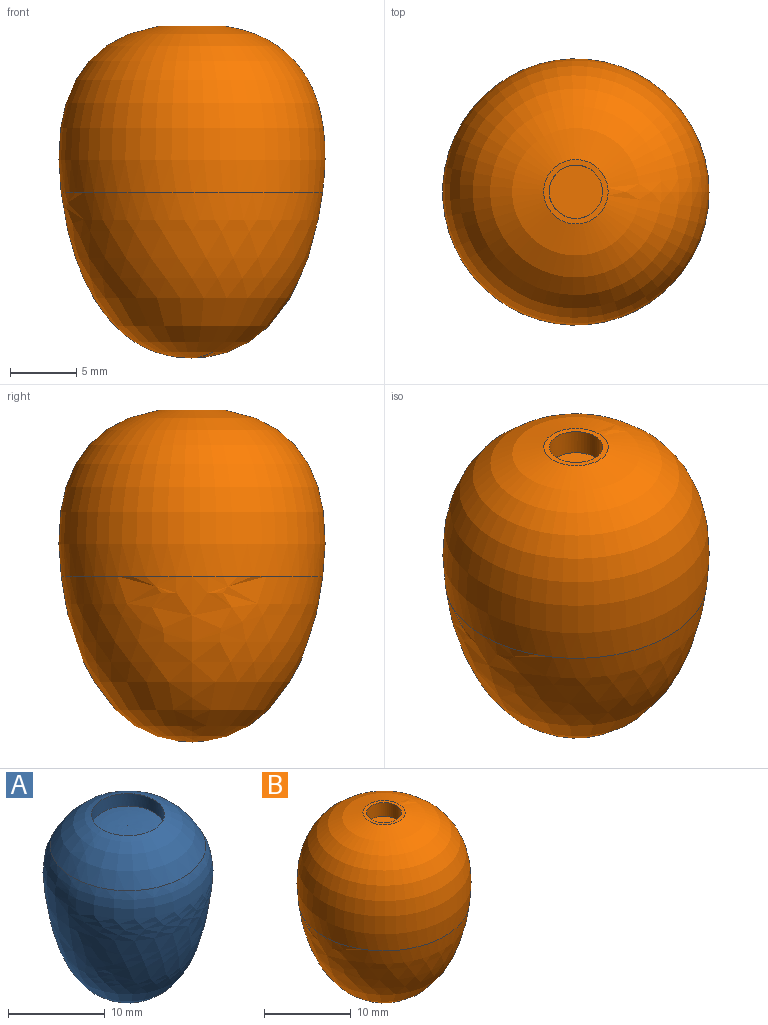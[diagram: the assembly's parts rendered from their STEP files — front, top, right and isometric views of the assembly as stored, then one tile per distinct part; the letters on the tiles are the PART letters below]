
ASSEMBLY  parts=2 mates=1
PART A: 6 faces, bbox 17.6x17.6x22.3 mm
  f0: revolved ~18.32x17.59mm, area 924.4mm2, adj f1
  f1: revolved ~16.06x16.06mm, area 231.2mm2, adj f0,f2
  f2: cylinder r=3.76mm len=7.53mm, axis (0,0,-1), area 37.4mm2, adj f1,f3
  f3: revolved ~7.53x7.53mm, area 44.7mm2, adj f2
  f4: revolved ~13.54x13.54mm, area 369.3mm2, adj f5
  f5: revolved ~12.8x12.8mm, area 341.3mm2, adj f4
PART B: 9 faces, bbox 20.1x20.1x25 mm
  f0: plane 4.86x4.86mm, normal (0,0,1), area 5.9mm2, adj f1,f3
  f1: revolved ~20.09x20.09mm, area 823.7mm2, adj f0,f2
  f2: revolved ~19.71x19.71mm, area 704.8mm2, adj f1
  f3: cylinder r=2.01mm len=4.02mm, axis (0,0,1), area 24.5mm2, adj f0,f4
  f4: plane 4.02x4.02mm, normal (0,0,1), area 12.7mm2, adj f3
  f5: revolved ~18.32x17.59mm, area 924.4mm2, adj f6
  f6: revolved ~16.06x16.06mm, area 231.2mm2, adj f5,f7
  f7: cylinder r=3.76mm len=7.53mm, axis (0,0,-1), area 37.4mm2, adj f6,f8
  f8: revolved ~7.53x7.53mm, area 44.7mm2, adj f7
PLACE A t=(0,19.98,2.12)mm
PLACE B t=(0,19.98,2.12)mm
MATE fastened B.f7 <-> A.f2  axis (0,0,1) through (0,19.98,2.12)mm
